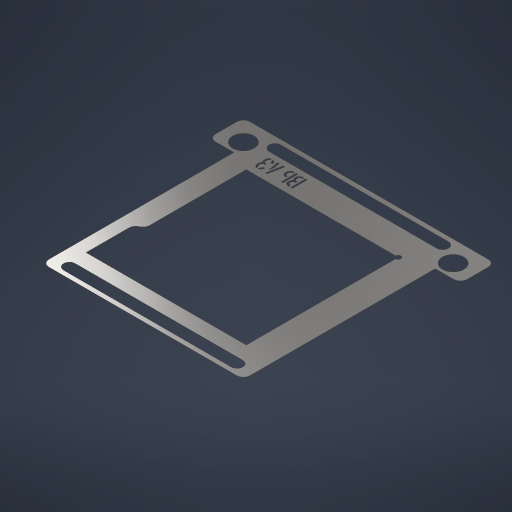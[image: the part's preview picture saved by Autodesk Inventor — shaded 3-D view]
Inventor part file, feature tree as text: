
AUTODESK INVENTOR PART (.ipt)
format: ipt  version: 2024 (Build 280153000, 153)  size: 454,144 bytes
history: native  units: in
note: dims shown in document units (in); Inventor stores cm internally (conversion verified against a paired STEP export)
features: extrude x5, sketch x2, hole x1, fillet x1, emboss x1
ambient origin geometry x8: Origin, YZ Plane, XZ Plane, XY Plane, X Axis, Y Axis, Z Axis, Center Point
bodies: Solid1 (feature_tree)
feature tree (10):
  extrude  "Extrusion1"  Depth=2.7in
  extrude  "Extrusion2"  TaperAngle=0.0deg  [1 undecoded]
  hole  "Hole1"  [1 undecoded]
  extrude  "Extrusion3"  Depth=0.4134in
  extrude  "Extrusion4"  Depth=0.1378in
  extrude  "Extrusion5"  Depth=0.1378in
  fillet  "Fillet2"  Radius=2.0in
  emboss  "Emboss2"
  sketch  "Sketch2"  dims[d0=3.0in d1=2.7in]
  sketch  "Sketch8"  dims[d2=0.002in d3=0.0in d7=0.0in d8=0.0in d13=2.1in d14=0.3in d16=0.4134in d17=0.1378in d18=0.1378in d19=2.0in d20=2.0in d21=0.125in d22=0.125in d23=1.0in d24=0.0in d27=0.0in d28=0.0in d29=0.0625in d34=1.811in d35=1.811in d36=0.5906in d37=0.0984in d38=0.0in d39=0.0in d41=0.25in d42=0.25in d43=0.25in d44=0.255in d45=0.2362in d46=0.219in d47=0.112in d48=0.5635in d49=0.315in d50=0.8108in d51=0.075in d52=0.225in d53=0.313in d54=0.0413in d55=0.0787in d58=0.0394in d59=0.0in]
note: 2 required parameter values undecoded (feature->parameter linkage not recoverable at this tier; creation-order binding heuristic only, values carry confidence <= 0.55)
